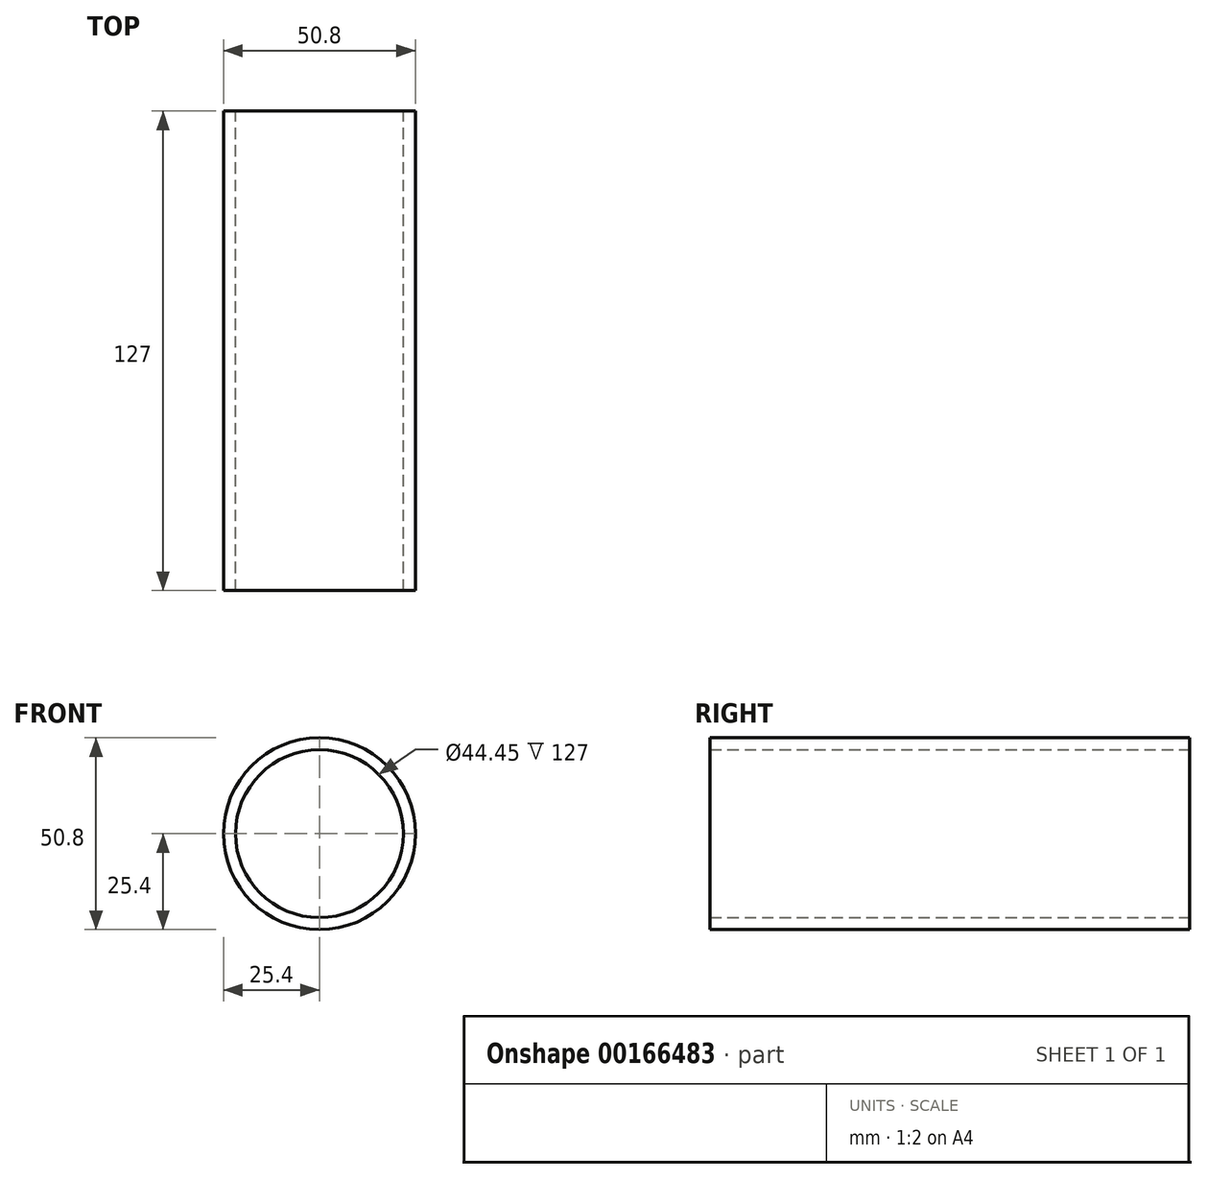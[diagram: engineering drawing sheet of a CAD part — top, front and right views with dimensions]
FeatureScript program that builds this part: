
annotation { "Feature Type Name" : "Feature", "Feature Type Description" : "" }
export const myFeature = defineFeature(function(context is Context, id is Id, definition is map)
    precondition{}
    {
        {
            var Q0;
            Q0=qCreatedBy(makeId("Front.planeOp"),FACE);
            var sketch = newSketch(context, id + "F0", { "sketchPlane" : qUnion([Q0])});
            skCircle(sketch, "E0", {"center": v(0, 0) * mm, "radius": 25.4 * mm});
            skCircle(sketch, "E1", {"center": v(0, 0) * mm, "radius": 22.23 * mm});
            skSolve(sketch);
        }
        {
            var Q0;
            Q0 = qSketchRegion(id + "F0", true);
            extrude(context, id + "F1", {"entities" : qUnion([Q0]), "depth" : 127 * mm});
        }
    });
